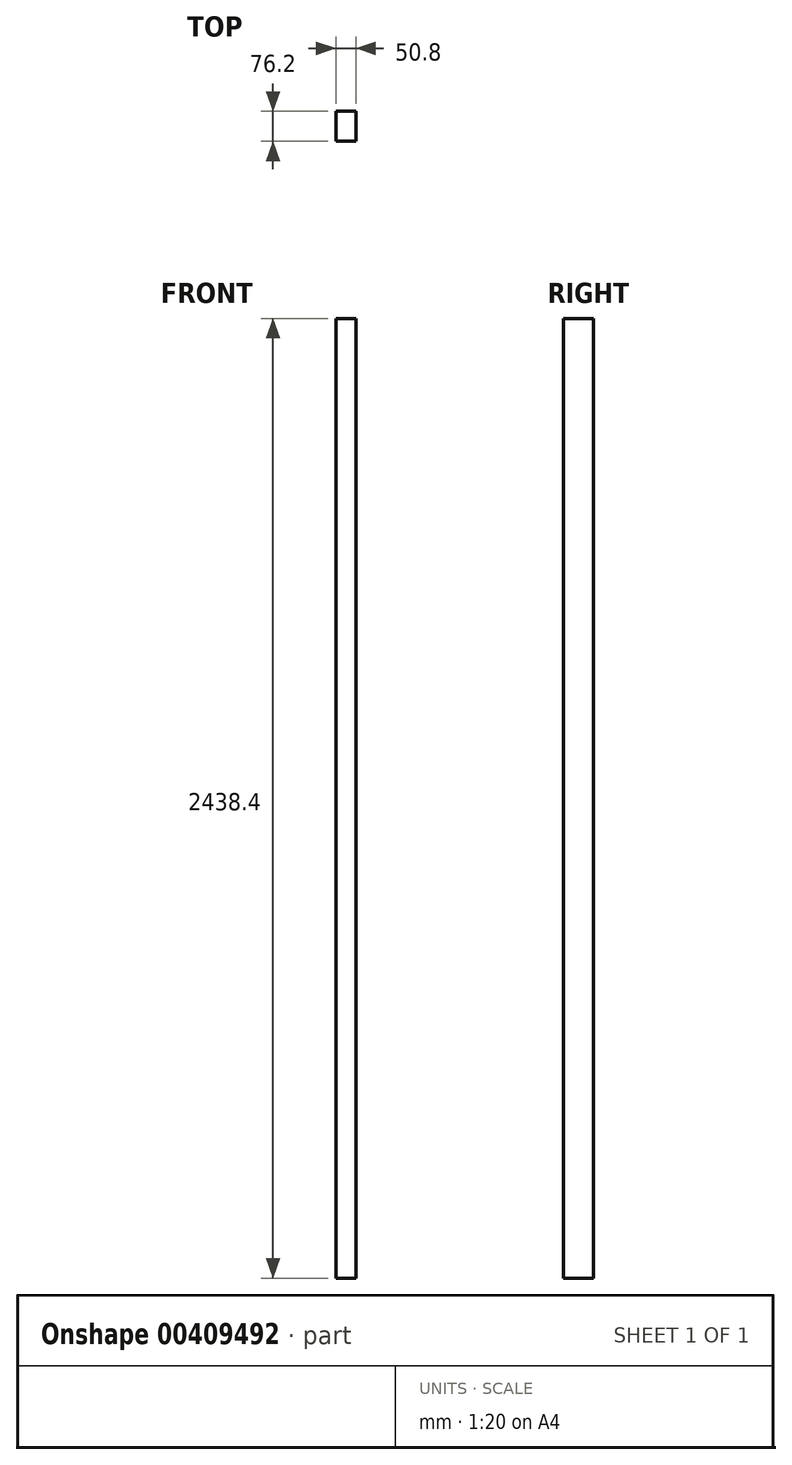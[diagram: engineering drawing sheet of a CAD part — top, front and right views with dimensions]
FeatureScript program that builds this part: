
annotation { "Feature Type Name" : "Feature", "Feature Type Description" : "" }
export const myFeature = defineFeature(function(context is Context, id is Id, definition is map)
    precondition{}
    {
        {
            var Q0;
            Q0=qCreatedBy(makeId("Front.planeOp"),FACE);
            var sketch = newSketch(context, id + "F0", { "sketchPlane" : qUnion([Q0])});
            skLineSegment(sketch, "E0.bottom", {"start": v(-25.4, 1219.2) * mm, "end": v(25.4, 1219.2) * mm});
            skLineSegment(sketch, "E0.top", {"start": v(-25.4, -1219.2) * mm, "end": v(25.4, -1219.2) * mm});
            skLineSegment(sketch, "E0.left", {"start": v(-25.4, 1219.2) * mm, "end": v(-25.4, -1219.2) * mm});
            skLineSegment(sketch, "E0.right", {"start": v(25.4, 1219.2) * mm, "end": v(25.4, -1219.2) * mm});
            skSolve(sketch);
        }
        {
            var Q0;
            Q0=makeQuery(id+"F0.imprint","IMPRINT",FACE,{"disambiguationData":[TD([[makeQuery(id+"F0.imprint","IMPRINT",EDGE,{"derivedFrom":sQuery(id+"F0.wireOp",EDGE,"E0.bottom")}),-1.0]])]});
            extrude(context, id + "F1", {"entities" : qUnion([Q0]), "depth" : 76.2 * mm});
        }
    });
